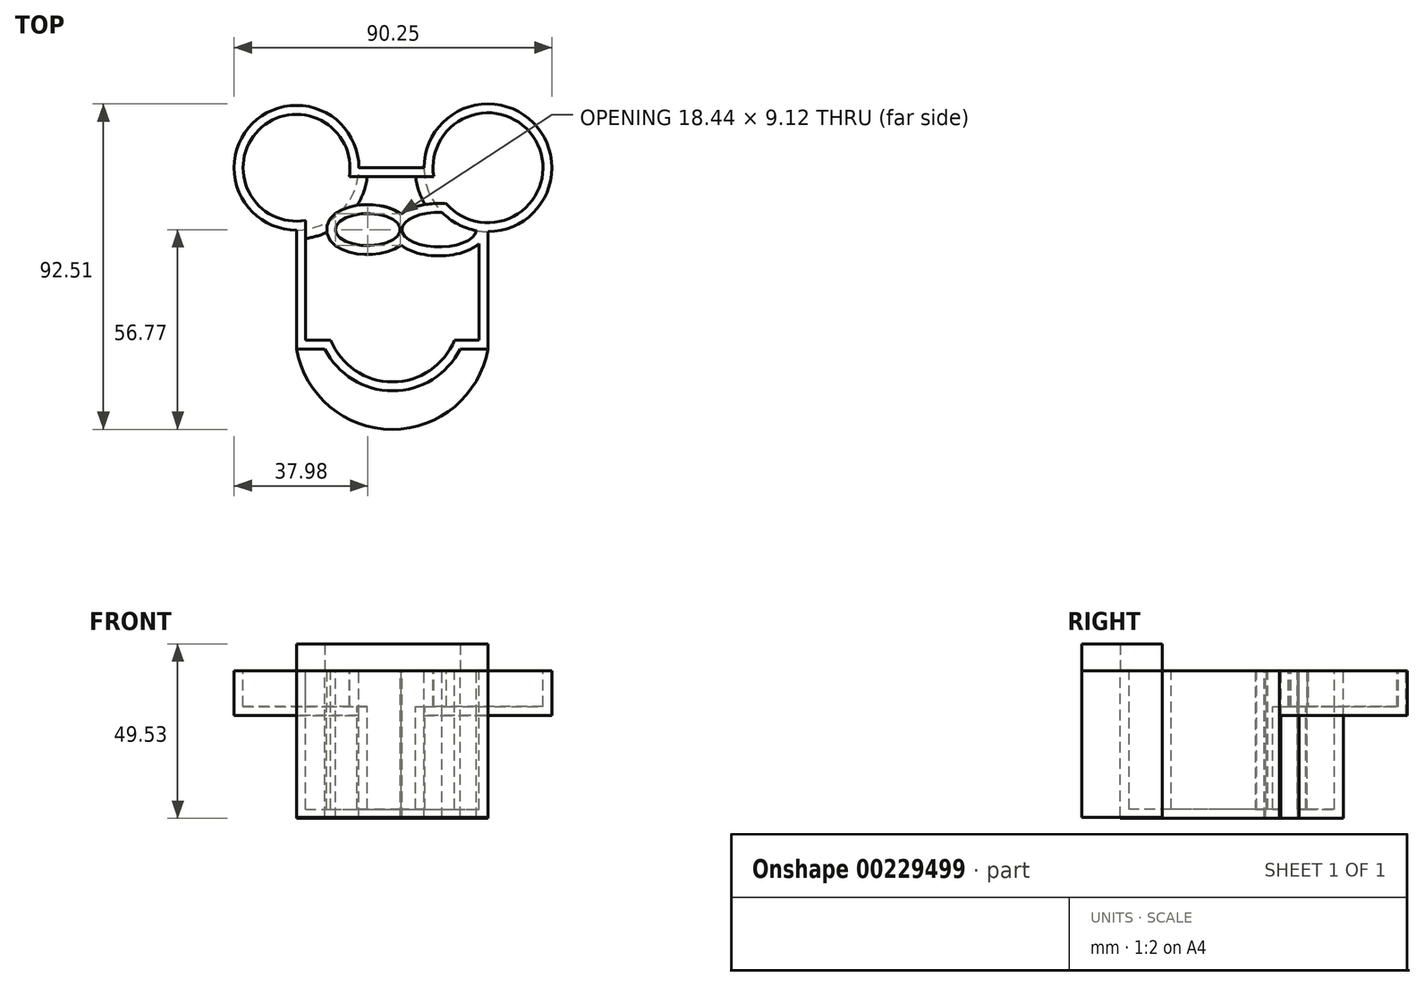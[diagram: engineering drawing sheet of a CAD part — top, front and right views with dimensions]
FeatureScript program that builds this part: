
annotation { "Feature Type Name" : "Feature", "Feature Type Description" : "" }
export const myFeature = defineFeature(function(context is Context, id is Id, definition is map)
    precondition{}
    {
        {
            var Q0;
            Q0=qCreatedBy(makeId("Top.planeOp"),FACE);
            var sketch = newSketch(context, id + "F0", { "sketchPlane" : qUnion([Q0])});
            skLineSegment(sketch, "E0.bottom", {"start": v(-2.54, 17.57) * mm, "end": v(15.95, 17.57) * mm});
            skLineSegment(sketch, "E0.top", {"start": v(-20.26, -33.9) * mm, "end": v(-12.2, -33.9) * mm});
            skLineSegment(sketch, "E0.left", {"start": v(-20.26, -0.15) * mm, "end": v(-20.26, -33.9) * mm});
            skLineSegment(sketch, "E0.right", {"start": v(34.11, -0.59) * mm, "end": v(34.11, -33.9) * mm});
            skCircle(sketch, "E1", {"center": v(-20.26, 17.57) * mm, "radius": 17.72 * mm});
            skCircle(sketch, "E2", {"center": v(34.11, 17.57) * mm, "radius": 18.16 * mm});
            skEllipse(sketch, "E3", {"center": v(0, 0) * mm, "majorRadius": 9.22 * mm, "minorRadius": 4.56 * mm, "majorAxis": v(-1, 0)});
            skEllipticalArc(sketch, "E4", {});
            skArc(sketch, "E5", {"start": v(-20.26, -33.9) * mm, "mid": v(6.93, -56.77) * mm, "end": v(34.11, -33.9) * mm});
            skArc(sketch, "E6", {"start": v(-12.2, -33.9) * mm, "mid": v(7.03, -45.82) * mm, "end": v(26.26, -33.9) * mm});
            skLineSegment(sketch, "E7.trimOffspring", {"start": v(26.26, -33.9) * mm, "end": v(34.11, -33.9) * mm});
            const initialGuessF0  = {"E4": [0.020260928198695183, 0, -1, 0, 0.010575984400069962, 0.004915279167947715, 4.632587344518667, 3.0831127346890574]};
            skSetInitialGuess(sketch, initialGuessF0);
            skSolve(sketch);
        }
        {
            var Q0;
            {var subQ2=sQuery(id+"F0.wireOp",EDGE,"E0.bottom");Q0=makeQuery(id+"F0.imprint","IMPRINT",FACE,{"disambiguationData":[TD([[makeQuery(id+"F0.imprint","IMPRINT",EDGE,{"derivedFrom":subQ2}),-1.0]])]});}
            extrude(context, id + "F1", {"entities" : qUnion([Q0]), "oppositeDirection" : true, "depth" : 41.9 * mm});
        }
        {
            var Q0;
            {var subQ0=sQuery(id+"F0.wireOp",EDGE,"E1");var subQ1=makeQuery(id+"F0.imprint","INTERSECT",VERTEX,{"derivedFrom":[sQuery(id+"F0.wireOp",EDGE,"E0.bottom"),subQ0]});Q0=makeQuery(id+"F0.imprint","IMPRINT",FACE,{"disambiguationData":[TD([[makeQuery(id+"F0.imprint","IMPRINT",EDGE,{"disambiguationData":[TD([[subQ1,-1.0]])],"derivedFrom":subQ0}),1.0]])]});}
            var Q1;
            {var subQ0=sQuery(id+"F0.wireOp",EDGE,"E2");var subQ1=makeQuery(id+"F0.imprint","INTERSECT",VERTEX,{"derivedFrom":[sQuery(id+"F0.wireOp",EDGE,"E0.bottom"),subQ0]});Q1=makeQuery(id+"F0.imprint","IMPRINT",FACE,{"disambiguationData":[TD([[makeQuery(id+"F0.imprint","IMPRINT",EDGE,{"disambiguationData":[TD([[subQ1,-1.0]])],"derivedFrom":subQ0}),1.0]])]});}
            extrude(context, id + "F2", {"entities" : qUnion([Q0, Q1]), "operationType" : NewBodyOperationType.ADD, "oppositeDirection" : true, "depth" : 12.7 * mm});
        }
        {
            var Q0;
            Q0=makeQuery(id+"F0.imprint","IMPRINT",FACE,{"disambiguationData":[TD([[makeQuery(id+"F0.imprint","IMPRINT",EDGE,{"derivedFrom":sQuery(id+"F0.wireOp",EDGE,"E0.top")}),-1.0]])]});
            extrude(context, id + "F3", {"entities" : qUnion([Q0]), "depth" : 7.62 * mm});
        }
        {
            var Q0;
            Q0=makeQuery(id+"F0.imprint","IMPRINT",FACE,{"disambiguationData":[TD([[makeQuery(id+"F0.imprint","IMPRINT",EDGE,{"derivedFrom":sQuery(id+"F0.wireOp",EDGE,"E0.top")}),-1.0]])]});
            extrude(context, id + "F4", {"entities" : qUnion([Q0]), "oppositeDirection" : true, "depth" : 41.66 * mm});
        }
        {
            var Q0;
            {var subQ0=sQuery(id+"F0.wireOp",EDGE,"E2");var subQ1=sQuery(id+"F0.wireOp",EDGE,"E1");Q0=makeQuery(id+"F2.boolean.opBoolean","MERGE",FACE,{"derivedFrom":[makeQuery(id+"F1.opExtrude","CAP_FACE",FACE,{"disambiguationData":[OSD([sQuery(id+"F0.wireOp",EDGE,"E0.bottom"),sQuery(id+"F0.wireOp",EDGE,"E0.top"),sQuery(id+"F0.wireOp",EDGE,"E0.left"),sQuery(id+"F0.wireOp",EDGE,"E0.right"),subQ1,subQ0,sQuery(id+"F0.wireOp",EDGE,"E3"),sQuery(id+"F0.wireOp",EDGE,"E4"),sQuery(id+"F0.wireOp",EDGE,"E6"),sQuery(id+"F0.wireOp",EDGE,"E7.trimOffspring")])],"isStart":true}),makeQuery(id+"F2.opExtrude","CAP_FACE",FACE,{"disambiguationData":[OSD([subQ1])],"isStart":true}),makeQuery(id+"F2.opExtrude","CAP_FACE",FACE,{"disambiguationData":[OSD([subQ0])],"isStart":true})]});}
            shell(context, id + "F5", {"entities" : qUnion([Q0]), "thickness" : 2.54 * mm});
        }
    });
